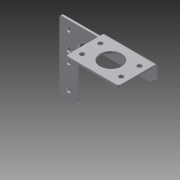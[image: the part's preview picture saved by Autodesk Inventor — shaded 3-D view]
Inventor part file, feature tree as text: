
AUTODESK INVENTOR PART (.ipt)
format: ipt  version: 2013 (Build 170138000, 138)  size: 231,424 bytes
history: native  units: in
note: dims shown in document units (in); Inventor stores cm internally (conversion verified against a paired STEP export)
features: sheet_metal_op x4, other x4, sketch x3, chamfer x1
ambient origin geometry x8: Origin, YZ Plane, XZ Plane, XY Plane, X Axis, Y Axis, Z Axis, Center Point
bodies: Solid1 (feature_tree)
feature tree (12):
  sheet_metal_op  "Face1"
  sheet_metal_op  "Flange1"
  chamfer  "Corner Round1"
  sketch  "Sketch1"  dims[d0=1.0in]
  other  "Plate1"
  sketch  "Sketch2"  dims[d2=0.26in]
  other  "Plate2"
  sheet_metal_op  "Bend1"
  sheet_metal_op  "Corner1"
  sketch  "Sketch3"  dims[d3=0.26in d4=2.0in d5=1.0in d6=4.5in d7=0.75in d8=3.0in d9=0.125in d10=0.12in d11=0.12in d12=0.06in d13=0.24in d14=0.12in d15=2.25in d16=90.0deg d17=0.05in d18=0.48in d19=0.12in d20=0.12in d21=0.5in d22=0.125in d23=0.26in d25=0.375in d26=0.5in d27=0.12in d28=0.0in d29=0.53in d30=0.395in d31=1.25in d32=2.0in d33=0.26in d34=0.5in d35=1.378in d1=0.0625in]
  other  "Cut1"
  other  "Definition1"
